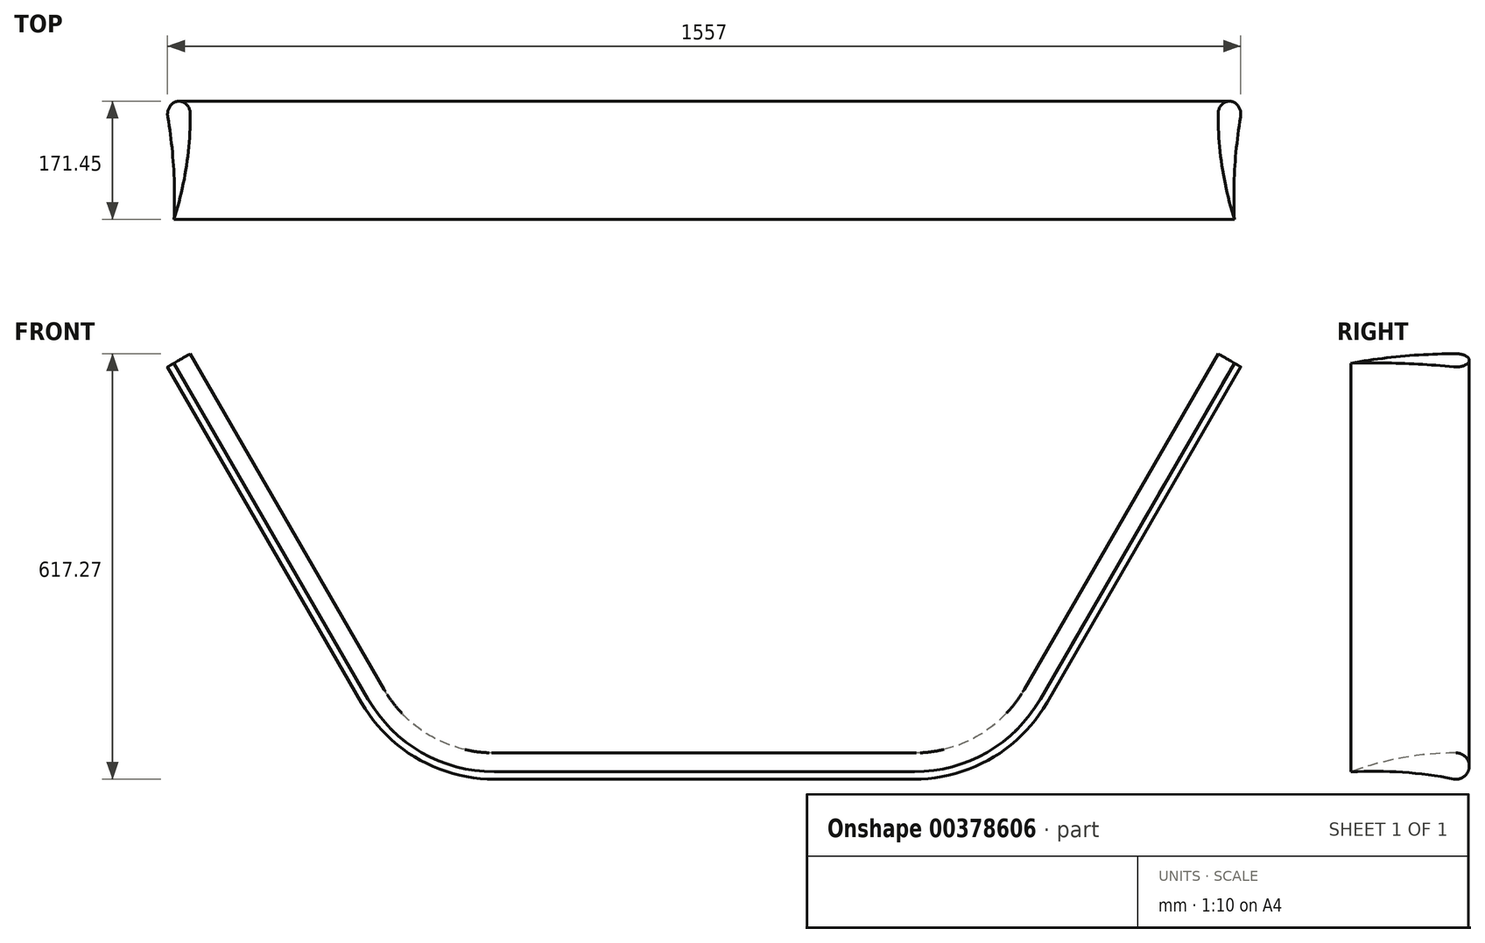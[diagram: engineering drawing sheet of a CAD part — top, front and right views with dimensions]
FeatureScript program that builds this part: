
annotation { "Feature Type Name" : "Feature", "Feature Type Description" : "" }
export const myFeature = defineFeature(function(context is Context, id is Id, definition is map)
    precondition{}
    {
        {
            var Q0;
            Q0=qCreatedBy(makeId("Front.planeOp"),FACE);
            var sketch = newSketch(context, id + "F0", { "sketchPlane" : qUnion([Q0])});
            skLineSegment(sketch, "E0", {"start": v(0, 0) * mm, "end": v(0, 557.68) * mm, "construction": true});
            skLineSegment(sketch, "E1", {"start": v(0, 0) * mm, "end": v(304.8, 0) * mm});
            skArc(sketch, "E2", {"start": v(304.8, 0) * mm, "mid": v(406.4, 27.22) * mm, "end": v(480.78, 101.6) * mm});
            skLineSegment(sketch, "E3", {"start": v(480.78, 101.6) * mm, "end": v(762, 588.7) * mm});
            skSolve(sketch);
        }
        {
            var Q0;
            Q0=qCreatedBy(makeId("Right.planeOp"),FACE);
            var sketch = newSketch(context, id + "F1", { "sketchPlane" : qUnion([Q0])});
            skArc(sketch, "E4", {"start": v(-3.64, -18.7) * mm, "mid": v(18.96, -1.81) * mm, "end": v(-0.03, 19.05) * mm});
            skArc(sketch, "E5", {"start": v(-0.03, 19.05) * mm, "mid": v(-77.42, 12.1) * mm, "end": v(-152.4, -8.31) * mm});
            skArc(sketch, "E6", {"start": v(-3.64, -18.7) * mm, "mid": v(-77.7, -8.95) * mm, "end": v(-152.4, -8.31) * mm});
            skLineSegment(sketch, "E7", {"start": v(0, 0) * mm, "end": v(-176.3, 0) * mm});
            skSolve(sketch);
        }
        {
            var Q0;
            Q0=makeQuery(id+"F1.imprint","IMPRINT",FACE,{"disambiguationData":[TD([[makeQuery(id+"F1.imprint","IMPRINT",EDGE,{"derivedFrom":sQuery(id+"F1.wireOp",EDGE,"E4")}),1.0]])]});
            var Q1;
            Q1=sQuery(id+"F0.wireOp",EDGE,"E1");
            var Q2;
            Q2=sQuery(id+"F0.wireOp",EDGE,"E2");
            var Q3;
            Q3=sQuery(id+"F0.wireOp",EDGE,"E3");
            sweep(context, id + "F2", {"profiles" : qUnion([Q0]), "path" : qUnion([Q1, Q2, Q3])});
        }
        {
            var Q0;
            Q0=makeQuery(id+"F2.opSweep","SWEPT_BODY",BODY,{"disambiguationData":[OSD([sQuery(id+"F0.wireOp",EDGE,"E3"),sQuery(id+"F1.wireOp",EDGE,"E4"),sQuery(id+"F1.wireOp",EDGE,"E5"),sQuery(id+"F1.wireOp",EDGE,"E6")])]});
            var Q1;
            Q1=qCreatedBy(makeId("Right.planeOp"),FACE);
            mirror(context, id + "F3", {"operationType" : NewBodyOperationType.ADD, "entities" : qUnion([Q0]), "mirrorPlane" : qUnion([Q1])});
        }
    });
